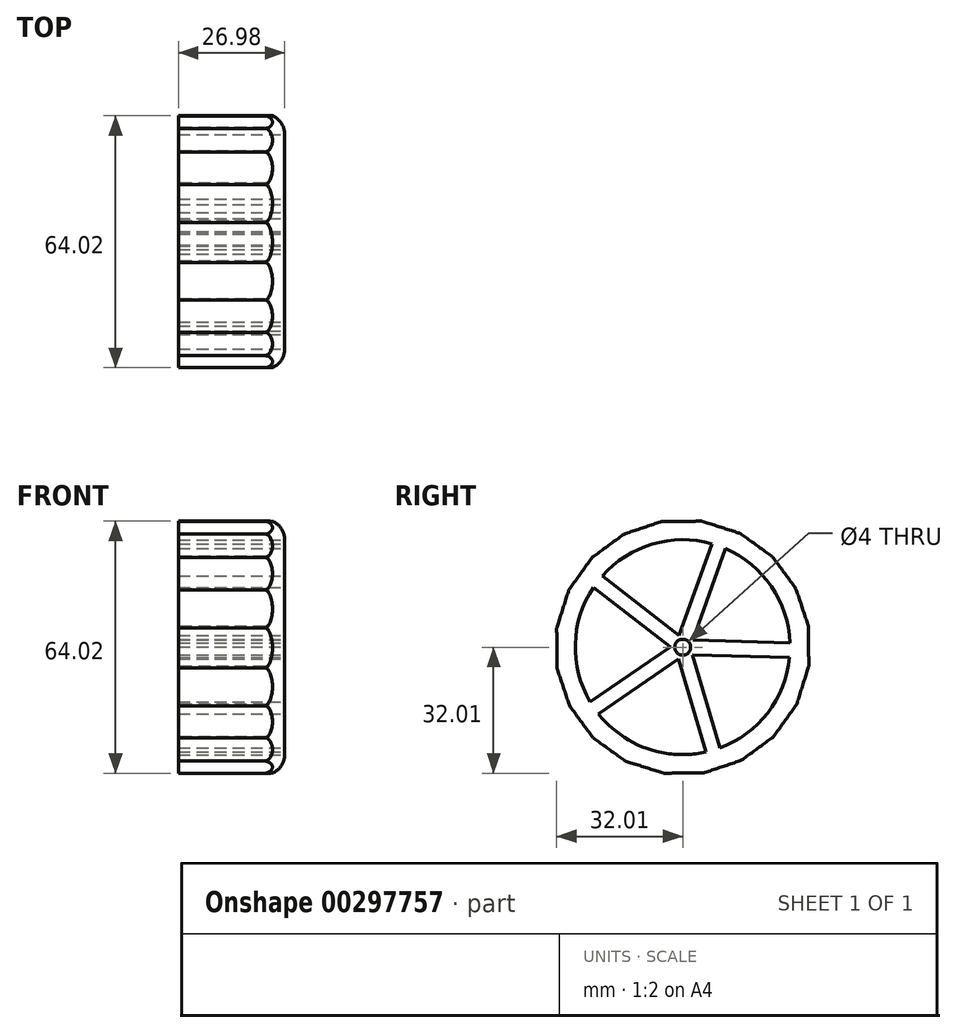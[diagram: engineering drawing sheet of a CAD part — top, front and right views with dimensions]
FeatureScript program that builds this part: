
annotation { "Feature Type Name" : "Feature", "Feature Type Description" : "" }
export const myFeature = defineFeature(function(context is Context, id is Id, definition is map)
    precondition{}
    {
        {
            var Q0;
            Q0=qCreatedBy(makeId("Right.planeOp"),FACE);
            var sketch = newSketch(context, id + "F0", { "sketchPlane" : qUnion([Q0])});
            skCircle(sketch, "E0", {"center": v(0, 0) * mm, "radius": 32.39 * mm});
            skSolve(sketch);
        }
        {
            var Q0;
            Q0 = qSketchRegion(id + "F0", true);
            extrude(context, id + "F1", {"entities" : qUnion([Q0]), "endBound" : BoundingType.SYMMETRIC, "depth" : 26.99 * mm});
        }
        {
            var Q0;
            Q0=makeQuery(id+"F1.opExtrude","CAP_EDGE",EDGE,{"disambiguationData":[OSD([sQuery(id+"F0.wireOp",EDGE,"E0")])],"isStart":false});
            fillet(context, id + "F2", {"entities" : qUnion([Q0]), "radius" : 5.08 * mm, "tangentPropagation" : true, "allowEdgeOverflow" : false});
        }
        {
            var Q0;
            Q0=makeQuery(id+"F1.opExtrude","CAP_FACE",FACE,{"disambiguationData":[OSD([sQuery(id+"F0.wireOp",EDGE,"E0")])],"isStart":false});
            var sketch = newSketch(context, id + "F3", { "sketchPlane" : qUnion([Q0])});
            skCircle(sketch, "E1", {"center": v(0, 0) * mm, "radius": 3.17 * mm});
            skCircle(sketch, "E2.cCircle", {"center": v(0, 0) * mm, "radius": 3.17 * mm, "construction": true});
            skLineSegment(sketch, "E2.0", {"start": v(-0.9, 3.05) * mm, "end": v(2.62, 1.8) * mm});
            skLineSegment(sketch, "E2.1", {"start": v(2.62, 1.8) * mm, "end": v(2.52, -1.94) * mm});
            skLineSegment(sketch, "E2.2", {"start": v(2.52, -1.94) * mm, "end": v(-1.07, -3) * mm});
            skLineSegment(sketch, "E2.3", {"start": v(-1.07, -3) * mm, "end": v(-3.17, 0.09) * mm});
            skLineSegment(sketch, "E2.4", {"start": v(-3.17, 0.09) * mm, "end": v(-0.9, 3.05) * mm});
            skLineSegment(sketch, "E3", {"start": v(-0.9, 3.05) * mm, "end": v(7.38, 26.29) * mm});
            skLineSegment(sketch, "E4", {"start": v(2.62, 1.8) * mm, "end": v(10.9, 25.04) * mm});
            skLineSegment(sketch, "E5", {"start": v(2.62, 1.8) * mm, "end": v(27.28, 1.1) * mm});
            skLineSegment(sketch, "E6", {"start": v(2.52, -1.94) * mm, "end": v(27.18, -2.63) * mm});
            skLineSegment(sketch, "E7", {"start": v(-1.07, -3) * mm, "end": v(5.9, -26.66) * mm});
            skLineSegment(sketch, "E8", {"start": v(-0.9, 3.05) * mm, "end": v(-20.44, 18.1) * mm});
            skLineSegment(sketch, "E9", {"start": v(-3.17, 0.09) * mm, "end": v(-22.72, 15.14) * mm});
            skLineSegment(sketch, "E10", {"start": v(-3.17, 0.09) * mm, "end": v(-23.53, -13.85) * mm});
            skLineSegment(sketch, "E11", {"start": v(-1.07, -3) * mm, "end": v(-21.42, -16.93) * mm});
            skLineSegment(sketch, "E12", {"start": v(2.52, -1.94) * mm, "end": v(9.48, -25.6) * mm});
            skCircle(sketch, "E13", {"center": v(0, 0) * mm, "radius": 2 * mm});
            skSolve(sketch);
        }
        {
            var Q0;
            {var subQ0=sQuery(id+"F3.wireOp",EDGE,"E6");Q0=makeQuery(id+"F3.imprint","IMPRINT",FACE,{"disambiguationData":[TD([[makeQuery(id+"F3.imprint","IMPRINT",EDGE,{"derivedFrom":subQ0}),-1.0]])]});}
            var Q1;
            {var subQ0=sQuery(id+"F3.wireOp",EDGE,"E4");Q1=makeQuery(id+"F3.imprint","IMPRINT",FACE,{"disambiguationData":[TD([[makeQuery(id+"F3.imprint","IMPRINT",EDGE,{"derivedFrom":subQ0}),-1.0]])]});}
            var Q2;
            {var subQ0=sQuery(id+"F3.wireOp",EDGE,"E3");Q2=makeQuery(id+"F3.imprint","IMPRINT",FACE,{"disambiguationData":[TD([[makeQuery(id+"F3.imprint","IMPRINT",EDGE,{"derivedFrom":subQ0}),1.0]])]});}
            var Q3;
            {var subQ0=sQuery(id+"F3.wireOp",EDGE,"E9");Q3=makeQuery(id+"F3.imprint","IMPRINT",FACE,{"disambiguationData":[TD([[makeQuery(id+"F3.imprint","IMPRINT",EDGE,{"derivedFrom":subQ0}),1.0]])]});}
            var Q4;
            {var subQ0=sQuery(id+"F3.wireOp",EDGE,"E7");Q4=makeQuery(id+"F3.imprint","IMPRINT",FACE,{"disambiguationData":[TD([[makeQuery(id+"F3.imprint","IMPRINT",EDGE,{"derivedFrom":subQ0}),-1.0]])]});}
            var Q5;
            Q5=makeQuery(id+"F3.imprint","IMPRINT",FACE,{"disambiguationData":[TD([[makeQuery(id+"F3.imprint","IMPRINT",EDGE,{"derivedFrom":sQuery(id+"F3.wireOp",EDGE,"E13")}),1.0]])]});
            extrude(context, id + "F4", {"entities" : qUnion([Q0, Q1, Q2, Q3, Q4, Q5]), "operationType" : NewBodyOperationType.REMOVE, "endBound" : BoundingType.UP_TO_NEXT, "oppositeDirection" : true, "depth" : 15.75 * mm});
        }
        {
            var Q0;
            Q0=makeQuery(id+"F1.opExtrude","CAP_FACE",FACE,{"disambiguationData":[OSD([sQuery(id+"F0.wireOp",EDGE,"E0")])],"isStart":true});
            var sketch = newSketch(context, id + "F5", { "sketchPlane" : qUnion([Q0])});
            skCircle(sketch, "E14.cCircle", {"center": v(0, 0) * mm, "radius": 32.39 * mm, "construction": true});
            skLineSegment(sketch, "E14.0", {"start": v(-28.77, 14.86) * mm, "end": v(-22.77, 23.02) * mm});
            skLineSegment(sketch, "E14.1", {"start": v(-22.77, 23.02) * mm, "end": v(-14.55, 28.93) * mm});
            skLineSegment(sketch, "E14.2", {"start": v(-14.55, 28.93) * mm, "end": v(-4.9, 32.01) * mm});
            skLineSegment(sketch, "E14.3", {"start": v(-4.9, 32.01) * mm, "end": v(5.24, 31.96) * mm});
            skLineSegment(sketch, "E14.4", {"start": v(5.24, 31.96) * mm, "end": v(14.86, 28.77) * mm});
            skLineSegment(sketch, "E14.5", {"start": v(14.86, 28.77) * mm, "end": v(23.02, 22.77) * mm});
            skLineSegment(sketch, "E14.6", {"start": v(23.02, 22.77) * mm, "end": v(28.93, 14.55) * mm});
            skLineSegment(sketch, "E14.7", {"start": v(28.93, 14.55) * mm, "end": v(32.01, 4.9) * mm});
            skLineSegment(sketch, "E14.8", {"start": v(32.01, 4.9) * mm, "end": v(31.96, -5.24) * mm});
            skLineSegment(sketch, "E14.9", {"start": v(31.96, -5.24) * mm, "end": v(28.77, -14.86) * mm});
            skLineSegment(sketch, "E14.10", {"start": v(28.77, -14.86) * mm, "end": v(22.77, -23.02) * mm});
            skLineSegment(sketch, "E14.11", {"start": v(22.77, -23.02) * mm, "end": v(14.55, -28.93) * mm});
            skLineSegment(sketch, "E14.12", {"start": v(14.55, -28.93) * mm, "end": v(4.9, -32.01) * mm});
            skLineSegment(sketch, "E14.13", {"start": v(4.9, -32.01) * mm, "end": v(-5.24, -31.96) * mm});
            skLineSegment(sketch, "E14.14", {"start": v(-5.24, -31.96) * mm, "end": v(-14.86, -28.77) * mm});
            skLineSegment(sketch, "E14.15", {"start": v(-14.86, -28.77) * mm, "end": v(-23.02, -22.77) * mm});
            skLineSegment(sketch, "E14.16", {"start": v(-23.02, -22.77) * mm, "end": v(-28.93, -14.55) * mm});
            skLineSegment(sketch, "E14.17", {"start": v(-28.93, -14.55) * mm, "end": v(-32.01, -4.9) * mm});
            skLineSegment(sketch, "E14.18", {"start": v(-32.01, -4.9) * mm, "end": v(-31.96, 5.24) * mm});
            skLineSegment(sketch, "E14.19", {"start": v(-31.96, 5.24) * mm, "end": v(-28.77, 14.86) * mm});
            skSolve(sketch);
        }
        {
            var Q0;
            {var subQ0=sQuery(id+"F5.wireOp",EDGE,"E14.3");Q0=makeQuery(id+"F5.imprint","IMPRINT",FACE,{"disambiguationData":[TD([[makeQuery(id+"F5.imprint","IMPRINT",EDGE,{"derivedFrom":subQ0}),1.0]])]});}
            var Q1;
            {var subQ0=sQuery(id+"F5.wireOp",EDGE,"E14.2");Q1=makeQuery(id+"F5.imprint","IMPRINT",FACE,{"disambiguationData":[TD([[makeQuery(id+"F5.imprint","IMPRINT",EDGE,{"derivedFrom":subQ0}),1.0]])]});}
            var Q2;
            {var subQ0=sQuery(id+"F5.wireOp",EDGE,"E14.1");Q2=makeQuery(id+"F5.imprint","IMPRINT",FACE,{"disambiguationData":[TD([[makeQuery(id+"F5.imprint","IMPRINT",EDGE,{"derivedFrom":subQ0}),1.0]])]});}
            var Q3;
            {var subQ0=sQuery(id+"F5.wireOp",EDGE,"E14.0");Q3=makeQuery(id+"F5.imprint","IMPRINT",FACE,{"disambiguationData":[TD([[makeQuery(id+"F5.imprint","IMPRINT",EDGE,{"derivedFrom":subQ0}),1.0]])]});}
            var Q4;
            {var subQ0=sQuery(id+"F5.wireOp",EDGE,"E14.19");Q4=makeQuery(id+"F5.imprint","IMPRINT",FACE,{"disambiguationData":[TD([[makeQuery(id+"F5.imprint","IMPRINT",EDGE,{"derivedFrom":subQ0}),1.0]])]});}
            var Q5;
            {var subQ0=sQuery(id+"F5.wireOp",EDGE,"E14.18");Q5=makeQuery(id+"F5.imprint","IMPRINT",FACE,{"disambiguationData":[TD([[makeQuery(id+"F5.imprint","IMPRINT",EDGE,{"derivedFrom":subQ0}),1.0]])]});}
            var Q6;
            {var subQ0=sQuery(id+"F5.wireOp",EDGE,"E14.17");Q6=makeQuery(id+"F5.imprint","IMPRINT",FACE,{"disambiguationData":[TD([[makeQuery(id+"F5.imprint","IMPRINT",EDGE,{"derivedFrom":subQ0}),1.0]])]});}
            var Q7;
            {var subQ0=sQuery(id+"F5.wireOp",EDGE,"E14.16");Q7=makeQuery(id+"F5.imprint","IMPRINT",FACE,{"disambiguationData":[TD([[makeQuery(id+"F5.imprint","IMPRINT",EDGE,{"derivedFrom":subQ0}),1.0]])]});}
            var Q8;
            {var subQ0=sQuery(id+"F5.wireOp",EDGE,"E14.14");Q8=makeQuery(id+"F5.imprint","IMPRINT",FACE,{"disambiguationData":[TD([[makeQuery(id+"F5.imprint","IMPRINT",EDGE,{"derivedFrom":subQ0}),1.0]])]});}
            var Q9;
            {var subQ0=sQuery(id+"F5.wireOp",EDGE,"E14.15");Q9=makeQuery(id+"F5.imprint","IMPRINT",FACE,{"disambiguationData":[TD([[makeQuery(id+"F5.imprint","IMPRINT",EDGE,{"derivedFrom":subQ0}),1.0]])]});}
            var Q10;
            {var subQ0=sQuery(id+"F5.wireOp",EDGE,"E14.13");Q10=makeQuery(id+"F5.imprint","IMPRINT",FACE,{"disambiguationData":[TD([[makeQuery(id+"F5.imprint","IMPRINT",EDGE,{"derivedFrom":subQ0}),1.0]])]});}
            var Q11;
            {var subQ0=sQuery(id+"F5.wireOp",EDGE,"E14.12");Q11=makeQuery(id+"F5.imprint","IMPRINT",FACE,{"disambiguationData":[TD([[makeQuery(id+"F5.imprint","IMPRINT",EDGE,{"derivedFrom":subQ0}),1.0]])]});}
            var Q12;
            {var subQ0=sQuery(id+"F5.wireOp",EDGE,"E14.11");Q12=makeQuery(id+"F5.imprint","IMPRINT",FACE,{"disambiguationData":[TD([[makeQuery(id+"F5.imprint","IMPRINT",EDGE,{"derivedFrom":subQ0}),1.0]])]});}
            var Q13;
            {var subQ0=sQuery(id+"F5.wireOp",EDGE,"E14.10");Q13=makeQuery(id+"F5.imprint","IMPRINT",FACE,{"disambiguationData":[TD([[makeQuery(id+"F5.imprint","IMPRINT",EDGE,{"derivedFrom":subQ0}),1.0]])]});}
            var Q14;
            {var subQ0=sQuery(id+"F5.wireOp",EDGE,"E14.9");Q14=makeQuery(id+"F5.imprint","IMPRINT",FACE,{"disambiguationData":[TD([[makeQuery(id+"F5.imprint","IMPRINT",EDGE,{"derivedFrom":subQ0}),1.0]])]});}
            var Q15;
            {var subQ0=sQuery(id+"F5.wireOp",EDGE,"E14.8");Q15=makeQuery(id+"F5.imprint","IMPRINT",FACE,{"disambiguationData":[TD([[makeQuery(id+"F5.imprint","IMPRINT",EDGE,{"derivedFrom":subQ0}),1.0]])]});}
            var Q16;
            {var subQ0=sQuery(id+"F5.wireOp",EDGE,"E14.7");Q16=makeQuery(id+"F5.imprint","IMPRINT",FACE,{"disambiguationData":[TD([[makeQuery(id+"F5.imprint","IMPRINT",EDGE,{"derivedFrom":subQ0}),1.0]])]});}
            var Q17;
            {var subQ0=sQuery(id+"F5.wireOp",EDGE,"E14.6");Q17=makeQuery(id+"F5.imprint","IMPRINT",FACE,{"disambiguationData":[TD([[makeQuery(id+"F5.imprint","IMPRINT",EDGE,{"derivedFrom":subQ0}),1.0]])]});}
            var Q18;
            {var subQ0=sQuery(id+"F5.wireOp",EDGE,"E14.4");Q18=makeQuery(id+"F5.imprint","IMPRINT",FACE,{"disambiguationData":[TD([[makeQuery(id+"F5.imprint","IMPRINT",EDGE,{"derivedFrom":subQ0}),1.0]])]});}
            var Q19;
            {var subQ0=sQuery(id+"F5.wireOp",EDGE,"E14.5");Q19=makeQuery(id+"F5.imprint","IMPRINT",FACE,{"disambiguationData":[TD([[makeQuery(id+"F5.imprint","IMPRINT",EDGE,{"derivedFrom":subQ0}),1.0]])]});}
            extrude(context, id + "F6", {"entities" : qUnion([Q0, Q1, Q2, Q3, Q4, Q5, Q6, Q7, Q8, Q9, Q10, Q11, Q12, Q13, Q14, Q15, Q16, Q17, Q18, Q19]), "operationType" : NewBodyOperationType.REMOVE, "oppositeDirection" : true, "depth" : 25.4 * mm});
        }
    });
